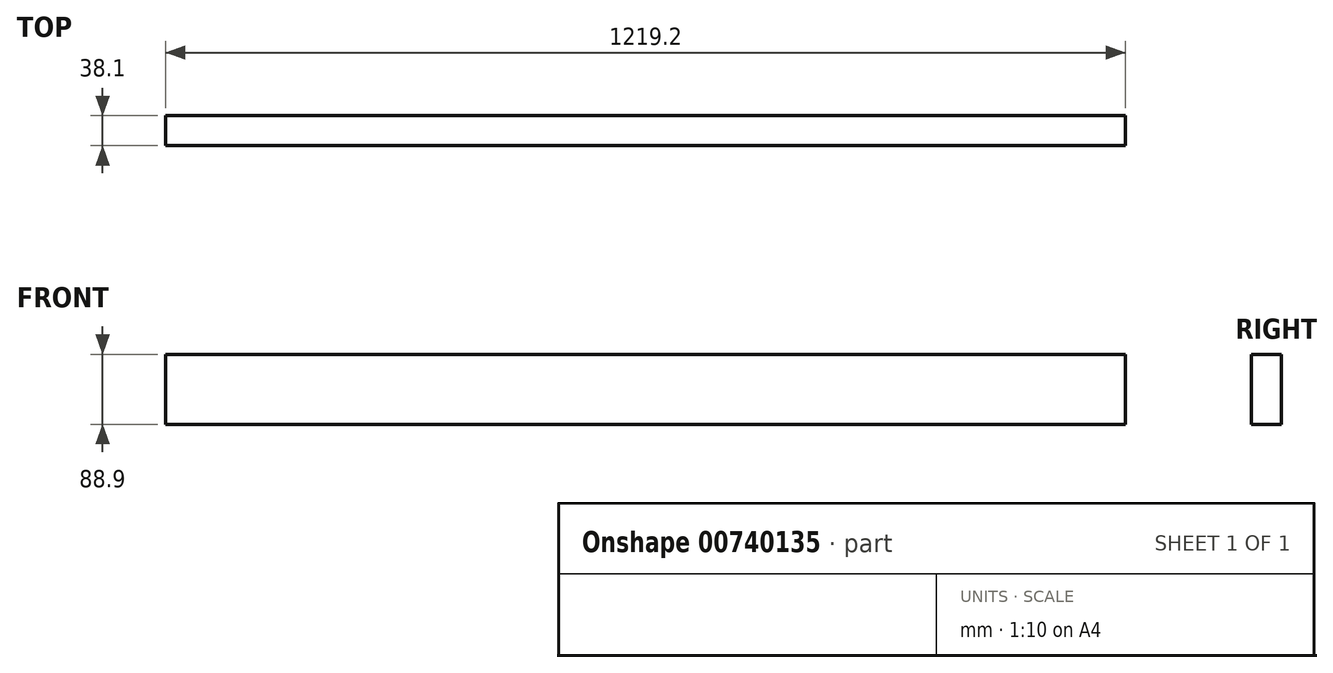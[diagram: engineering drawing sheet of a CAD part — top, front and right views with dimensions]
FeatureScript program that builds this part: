
annotation { "Feature Type Name" : "Feature", "Feature Type Description" : "" }
export const myFeature = defineFeature(function(context is Context, id is Id, definition is map)
    precondition{}
    {
        {
            var Q0;
            Q0=qCreatedBy(makeId("Right.planeOp"),FACE);
            var sketch = newSketch(context, id + "F0", { "sketchPlane" : qUnion([Q0])});
            skLineSegment(sketch, "E0.bottom", {"start": v(-79.68, 85.36) * mm, "end": v(-41.58, 85.36) * mm});
            skLineSegment(sketch, "E0.top", {"start": v(-79.68, -3.54) * mm, "end": v(-41.58, -3.54) * mm});
            skLineSegment(sketch, "E0.left", {"start": v(-79.68, 85.36) * mm, "end": v(-79.68, -3.54) * mm});
            skLineSegment(sketch, "E0.right", {"start": v(-41.58, 85.36) * mm, "end": v(-41.58, -3.54) * mm});
            skSolve(sketch);
        }
        {
            var Q0;
            Q0=makeQuery(id+"F0.imprint","IMPRINT",FACE,{"disambiguationData":[TD([[makeQuery(id+"F0.imprint","IMPRINT",EDGE,{"derivedFrom":sQuery(id+"F0.wireOp",EDGE,"E0.bottom")}),-1.0]])]});
            extrude(context, id + "F1", {"entities" : qUnion([Q0]), "depth" : 1219.2 * mm, "offsetDistance" : 25.4 * mm});
        }
    });
